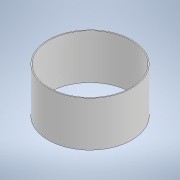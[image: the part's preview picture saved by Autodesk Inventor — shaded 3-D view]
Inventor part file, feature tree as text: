
AUTODESK INVENTOR PART (.ipt)
format: ipt  version: 2020.1 (Build 241239000, 239)  size: 102,912 bytes
history: native  units: mm
features: other x1, extrude x1, sketch x1
ambient origin geometry x8: Origin, YZ Plane, XZ Plane, XY Plane, X Axis, Y Axis, Z Axis, Center Point
bodies: Body1 (feature_tree)
feature tree (3):
  other  "Твердое тело1"
  extrude  "Выдавливание1"  Depth=18.2mm
  sketch  "Эскиз1"
